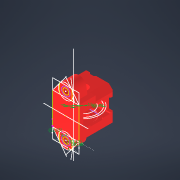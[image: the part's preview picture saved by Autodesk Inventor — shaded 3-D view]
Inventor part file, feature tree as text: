
AUTODESK INVENTOR PART (.ipt)
format: ipt  version: 2022.1 (Build 261234000, 234)  size: 681,984 bytes
history: native  units: mm
features: extrude x21, projected_geometry x20, sketch x18, reference x11, chamfer x7, delete_face x4, move_body x4, direct_edit x3, fillet x3, other x3, plane x1, hole x1
ambient origin geometry x8: Origin, YZ Plane, XZ Plane, XY Plane, X Axis, Y Axis, Z Axis, Center Point
bodies: Volumenkörper1 (feature_tree)
feature tree (96):
  extrude  "Extrusion1"  Depth=18.0mm
  extrude  "Extrusion2"  Depth=5.0mm
  plane  "Arbeitsebene1"
  extrude  "Extrusion3"  Depth=16.0mm
  extrude  "Extrusion4"  Depth=10.0mm
  extrude  "Extrusion5"  Depth=10.0mm
  hole  "Bohrung1"  [1 undecoded]
  extrude  "Extrusion6"  Depth=30.0mm
  chamfer  "Fase1"  Distance=7.5mm
  direct_edit  "Direktbearbeitung1"
  direct_edit  "Direktbearbeitung2"
  extrude  "Extrusion7"  TaperAngle=0.0deg  [1 undecoded]
  delete_face  "Fläche löschen1"
  delete_face  "Fläche löschen2"
  chamfer  "Fase8"  Distance=1.0mm Angle=45.0deg
  direct_edit  "Direktbearbeitung4"
  sketch  "Skizze11"  dims[d21=3.3mm d22=6.0mm d23=4.8mm d24=3.8mm d25=90.0deg d26=8.0mm d27=0.0mm d30=0.0mm d31=0.0mm d34=1.0mm d35=2.0mm d36=45.0deg]
  extrude  "Extrusion9"  TaperAngle=0.0deg  [1 undecoded]
  extrude  "Extrusion10"  Depth=10.0mm
  chamfer  "Fase10"  Distance=10.0mm
  extrude  "Extrusion13"  TaperAngle=0.0deg  [1 undecoded]
  extrude  "Extrusion19"  Depth=8.4mm
  extrude  "Extrusion20"  Depth=9.272952mm
  sketch  "Skizze20"  dims[d99=0.0mm d100=0.0mm d101=-0.25mm d106=8.4mm]
  extrude  "Extrusion21"  TaperAngle=0.0deg  [1 undecoded]
  extrude  "Extrusion22"  Depth=0.4mm
  extrude  "Extrusion23"  TaperAngle=90.0deg  [1 undecoded]
  extrude  "Extrusion24"  Depth=0.8mm
  extrude  "Extrusion25"  Depth=18.0mm TaperAngle=0.0deg
  chamfer  "Fase22"  Distance=3.0mm
  chamfer  "Fase23"  Distance=3.0mm
  fillet  "Rundung12"  Radius=11.0mm
  fillet  "Rundung13"  Radius=16.0mm
  extrude  "Extrusion26"  Depth=18.0mm
  chamfer  "Fase24"  Distance=10.5mm
  extrude  "Extrusion27"  Depth=18.0mm TaperAngle=0.0deg
  extrude  "Extrusion28"  Depth=18.0mm TaperAngle=0.0deg
  chamfer  "Fase25"  Distance=7.2mm
  fillet  "Rundung14"  Radius=5.0mm
  extrude  "Extrusion29"  Depth=18.0mm
  delete_face  "Fläche löschen5"
  delete_face  "Fläche löschen6"
  sketch  "Skizze1"  dims[d0=15.0mm d1=18.0mm]
  sketch  "Skizze2"  dims[d2=24.0mm d3=0.0mm d5=5.0mm]
  sketch  "Skizze3"  dims[d6=0.0mm d7=0.0mm d8=16.0mm]
  sketch  "Skizze4"  dims[d9=18.0mm d10=10.0mm]
  projected_geometry  "Projizierte Kontur1"
  projected_geometry  "Projizierte Kontur2"
  sketch  "Skizze5"  dims[d11=10.0mm d12=0.0mm d13=10.0mm]
  projected_geometry  "Projizierte Kontur3"
  projected_geometry  "Projizierte Kontur4"
  projected_geometry  "Projizierte Kontur5"
  sketch  "Skizze7"  dims[d14=1.5mm d15=0.0mm d16=0.0mm]
  reference  "Referenz1"
  reference  "Referenz2"
  reference  "Referenz3"
  reference  "Referenz4"
  reference  "Referenz5"
  reference  "Referenz6"
  reference  "Referenz7"
  reference  "Referenz8"
  reference  "Referenz9"
  reference  "Referenz10"
  reference  "Referenz11"
  sketch  "Skizze8"  dims[d17=7.0mm d18=30.0mm d19=7.5mm d20=0.0mm]
  projected_geometry  "Projizierte Kontur6"
  projected_geometry  "Projizierte Kontur7"
  projected_geometry  "Projizierte Kontur8"
  projected_geometry  "Projizierte Kontur10"
  sketch  "Skizze13"  dims[d40=0.0mm d41=0.0mm d42=-0.05mm d43=0.0mm d44=0.0mm d45=-0.05mm]
  projected_geometry  "Projizierte Kontur11"
  sketch  "Skizze18"  dims[d46=3.0mm d47=3.0mm d48=10.0mm d49=0.0mm]
  projected_geometry  "Projizierte Kontur17"
  sketch  "Skizze19"  dims[d93=0.4mm d94=2.0mm d95=45.0deg d96=0.0mm d97=0.0mm d98=-0.25mm]
  projected_geometry  "Projizierte Kontur18"
  sketch  "Skizze21"  dims[d107=9.272952mm d109=9.272952mm]
  projected_geometry  "Projizierte Kontur19"
  projected_geometry  "Projizierte Kontur20"
  sketch  "Skizze22"  dims[d110=10.0mm d111=0.0mm d112=0.0mm d113=0.0mm]
  projected_geometry  "Projizierte Kontur21"
  sketch  "Skizze23"  dims[d114=0.4mm d115=2.0mm d116=45.0deg d123=17.453293mm]
  projected_geometry  "Projizierte Kontur22"
  projected_geometry  "Projizierte Kontur23"
  sketch  "Skizze24"  dims[d124=135.0deg d125=90.0deg]
  projected_geometry  "Projizierte Kontur24"
  projected_geometry  "Projizierte Kontur25"
  sketch  "Skizze25"  dims[d126=1.6mm d127=0.8mm]
  projected_geometry  "Projizierte Kontur26"
  sketch  "Skizze26"  dims[d128=1.0mm d129=10.5mm d130=0.0mm d184=3.0mm d185=0.0mm d186=3.0mm d187=0.0mm d188=11.0mm d189=16.0mm d190=18.0mm d191=10.5mm d192=0.0mm d193=9.5mm d194=0.0mm d195=7.2mm d196=0.0mm d197=7.2mm d198=0.0mm d199=5.0mm d200=18.0mm d201=9.0mm d203=2.5mm d204=8.0mm d205=15.0mm d206=7.5mm d207=0.0mm d208=0.4mm d209=2.0mm d210=45.0deg d211=0.5mm d212=2.0mm d213=45.0deg d214=4.0mm d215=4.0mm d216=0.8mm d217=0.8mm d218=0.8mm d219=0.8mm d220=9.5mm d221=0.0mm d222=0.4mm d223=2.0mm d224=45.0deg d225=0.8mm d226=0.8mm d227=0.8mm d228=0.8mm d229=9.5mm d230=0.0mm d231=0.8mm d232=0.8mm d233=9.5mm d234=0.0mm d235=0.4mm d236=2.0mm d237=45.0deg d238=0.4mm d239=5.15mm d240=18.0mm d241=0.0mm]
  other  "<userpath>\Desktop\Voron-2-2.4r1\Custom\Front_Idlers\Baugruppe1.iam"
  other  "Baugruppe1.iam"
  other  "Front_Idler1:1"
  move_body  "Verschieben1"
  move_body  "Verschieben2"
  move_body  "Verschieben9"
  move_body  "Verschieben10"
note: 6 required parameter values undecoded (feature->parameter linkage not recoverable at this tier; creation-order binding heuristic only, values carry confidence <= 0.55)
